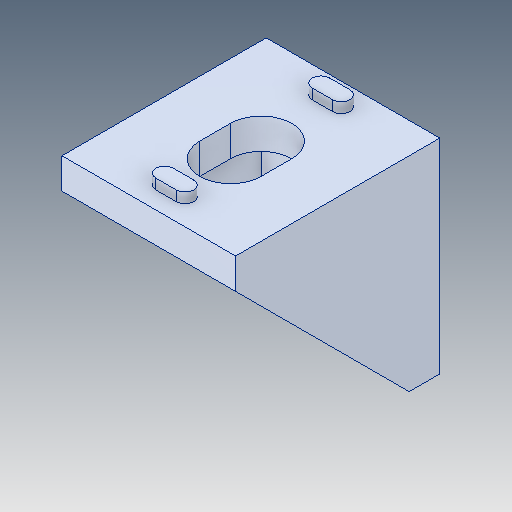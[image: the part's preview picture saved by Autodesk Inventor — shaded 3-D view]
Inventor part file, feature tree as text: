
AUTODESK INVENTOR PART (.ipt)
format: ipt  version: 2017 (Build 210142000, 142)  size: 145,408 bytes
history: mixed  units: mm
features: mirror x1, imported_body x1
ambient origin geometry x8: Origin, YZ Plane, XZ Plane, XY Plane, X Axis, Y Axis, Z Axis, Center Point
bodies: Solid1 (imported_parasolid)
feature tree (2):
  mirror  "Mirror1"
  imported_body  NMx_Import_Brep_tag  [imported B-rep: ~40 faces, bbox_mm=[17.0, 21.0, 21.0]]
